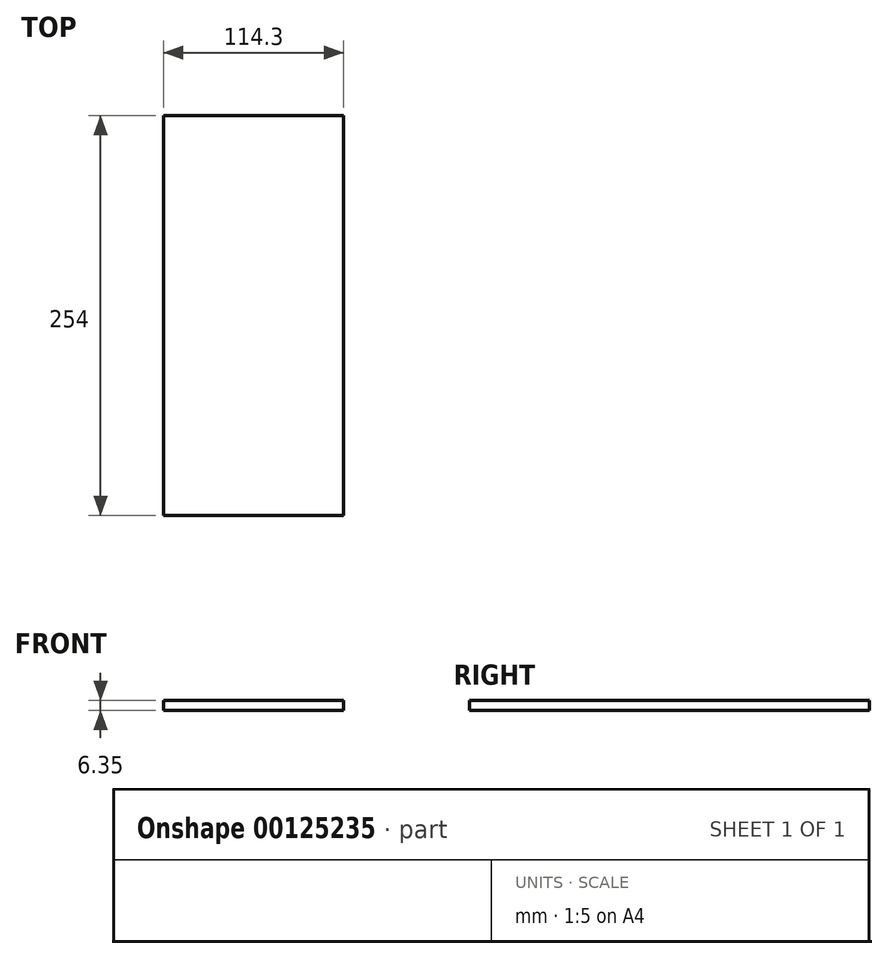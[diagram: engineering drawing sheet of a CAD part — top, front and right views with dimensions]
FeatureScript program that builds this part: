
annotation { "Feature Type Name" : "Feature", "Feature Type Description" : "" }
export const myFeature = defineFeature(function(context is Context, id is Id, definition is map)
    precondition{}
    {
        {
            var Q0;
            Q0=qCreatedBy(makeId("Top.planeOp"),FACE);
            var sketch = newSketch(context, id + "F0", { "sketchPlane" : qUnion([Q0])});
            skLineSegment(sketch, "E0.bottom", {"start": v(57.15, 127) * mm, "end": v(-57.15, 127) * mm});
            skLineSegment(sketch, "E0.top", {"start": v(57.15, -127) * mm, "end": v(-57.15, -127) * mm});
            skLineSegment(sketch, "E0.left", {"start": v(57.15, 127) * mm, "end": v(57.15, -127) * mm});
            skLineSegment(sketch, "E0.right", {"start": v(-57.15, 127) * mm, "end": v(-57.15, -127) * mm});
            skPoint(sketch, "E0.middle", {"position": v(0, 0) * mm});
            skSolve(sketch);
        }
        {
            var Q0;
            Q0=makeQuery(id+"F0.imprint","IMPRINT",FACE,{"disambiguationData":[TD([[makeQuery(id+"F0.imprint","IMPRINT",EDGE,{"derivedFrom":sQuery(id+"F0.wireOp",EDGE,"E0.bottom")}),1.0]])]});
            var Q1;
            Q1=qSketchRegion(id+"F0",true);
            extrude(context, id + "F1", {"entities" : qUnion([Q0, Q1]), "depth" : 6.35 * mm});
        }
    });
